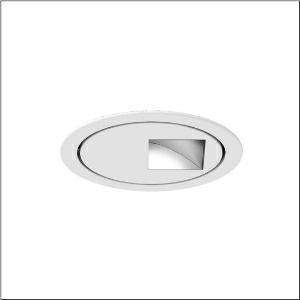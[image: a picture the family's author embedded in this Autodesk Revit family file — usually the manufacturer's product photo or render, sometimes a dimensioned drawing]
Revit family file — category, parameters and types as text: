
# Revit family: lunis_11_mini_round_51dk11cd2wg21
name_source: partatom
category: Lighting Fixtures
units: mm (PartAtom-declared; Revit-internal decimal feet)

## family parameters
Cut with Voids When Loaded = No
Host = Face
Light Source = No
Part Type = Normal
Room Calculation Point = No
Round Connector Dimension = Use Diameter
Shared = No

## types (1)
- Lunis 11 mini round (1 x LED 4000K / CRI = 80 (unbekannt), 2470 lm, 4000K)
    Apparent Load = 28 VA
    CIE Flux Codes = 44 77 97 100 100
    Color Rendering = 80
    Color Temperature = 4000K
    Default Elevation = 1800 mm
    Description = Lunis 11 mini round, downlight, light control with wallwasher, of highly reflective aluminium, highly specular, light emission: direct distribution, LED rated luminous flux: 2.470lm, light colour: 840, control gear: ECG, with terminal, 5-pole, mains connection: 220..230V, AC/DC, 0/50..60Hz, LED module, luminaire module, of aluminium, highly specular, white, diameter: 176mm, clamping range: 1..40mm, recessing ring, of plastic, traffic white (RAL 9016), protection rating (complete): IP20, insulation class (complete): insulation class II (safety insulation), certification: CE, permissible ambient temperature for indoor applications: 0..+35°C, packaging unit: 1 piece
    Height = 0 mm  [stored 0 ft]
    Lamp = 1 x LED 4000K / CRI >= 80 (unbekannt)
    Lamp Light Flux = 2470 lm
    Lamp count = 1
    Length = 176 mm
    Luminous efficacy = 89 lm/W
    Manufacturer = Siteco
    ModVariant = No
    Model = 51DK11CD2WG21
    Mounting Place = Ceiling
    Mounting Type = Recessed
    Number of Poles = 1
    OnlyDefault = Yes
    Power Factor = 1
    Product Name = Lunis 11 mini round
    Product group = downlight
    ProductGroupID = 400
    Protection Class = Protection class II
    Protection Degree = IP 20
    RLX_Detail_Level = 1
    RLX_Emergency_Light_Flux = 0 lm
    RLX_Emergency_Type = 0
    RLX_Emergency_Type_DB = No
    RlxData = <blob elided: 59289 chars, md5=979d0d4c>
    Socket = socket
    Standby Power = 0 W
    System Light Flux = 2470 lm
    System Power = 28 W
    Type Comments = Product without accessories
    Type Image = l_1004772.jpg
    URL = http://relux.com
    VarID = ---
    Voltage = 0 V
    Weight = 0.00 kg
    Width = 176 mm

note: [stored X ft] marks values corroborated as IEEE doubles in the binary element streams (Revit-internal decimal feet)

## geometry (parser evidence)
native form markers: Blend x4, Sweep x11
no freeform markers — native parametric forms only
